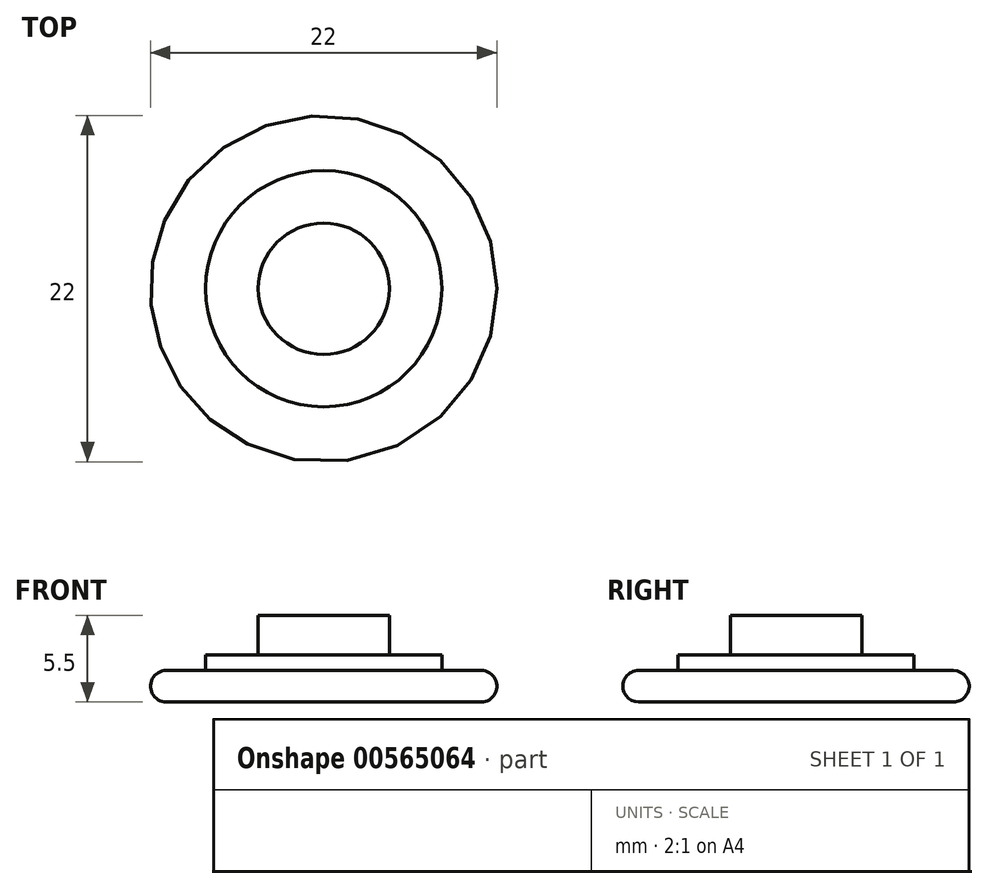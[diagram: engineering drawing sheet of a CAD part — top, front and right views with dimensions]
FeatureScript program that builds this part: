
annotation { "Feature Type Name" : "Feature", "Feature Type Description" : "" }
export const myFeature = defineFeature(function(context is Context, id is Id, definition is map)
    precondition{}
    {
        {
            var Q0;
            Q0=qCreatedBy(makeId("Top.planeOp"),FACE);
            var sketch = newSketch(context, id + "F0", { "sketchPlane" : qUnion([Q0])});
            skCircle(sketch, "E0", {"center": v(0, 0) * mm, "radius": 11 * mm});
            skCircle(sketch, "E1", {"center": v(0, 0) * mm, "radius": 7.5 * mm});
            skCircle(sketch, "E2", {"center": v(0, 0) * mm, "radius": 4.17 * mm});
            skSolve(sketch);
        }
        {
            var Q0;
            Q0=makeQuery(id+"F0.imprint","IMPRINT",FACE,{"disambiguationData":[TD([[makeQuery(id+"F0.imprint","IMPRINT",EDGE,{"derivedFrom":sQuery(id+"F0.wireOp",EDGE,"E0")}),1.0]])]});
            extrude(context, id + "F1", {"entities" : qUnion([Q0]), "depth" : 2 * mm, "offsetDistance" : 25 * mm});
        }
        {
            var Q0;
            Q0=makeQuery(id+"F0.imprint","IMPRINT",FACE,{"disambiguationData":[TD([[makeQuery(id+"F0.imprint","IMPRINT",EDGE,{"derivedFrom":sQuery(id+"F0.wireOp",EDGE,"E1")}),1.0]])]});
            extrude(context, id + "F2", {"entities" : qUnion([Q0]), "operationType" : NewBodyOperationType.ADD, "depth" : 3 * mm, "offsetDistance" : 25 * mm});
        }
        {
            var Q0;
            Q0=makeQuery(id+"F0.imprint","IMPRINT",FACE,{"disambiguationData":[TD([[makeQuery(id+"F0.imprint","IMPRINT",EDGE,{"derivedFrom":sQuery(id+"F0.wireOp",EDGE,"E2")}),1.0]])]});
            extrude(context, id + "F3", {"entities" : qUnion([Q0]), "operationType" : NewBodyOperationType.ADD, "depth" : 5.5 * mm, "offsetDistance" : 25 * mm});
        }
        {
            var Q0;
            Q0=makeQuery(id+"F1.opExtrude","CAP_EDGE",EDGE,{"disambiguationData":[OSD([sQuery(id+"F0.wireOp",EDGE,"E0")])],"isStart":false});
            var Q1;
            Q1=makeQuery(id+"F1.opExtrude","CAP_EDGE",EDGE,{"disambiguationData":[OSD([sQuery(id+"F0.wireOp",EDGE,"E0")])],"isStart":true});
            fillet(context, id + "F4", {"entities" : qUnion([Q0, Q1]), "radius" : 1 * mm, "tangentPropagation" : true, "allowEdgeOverflow" : false});
        }
    });
